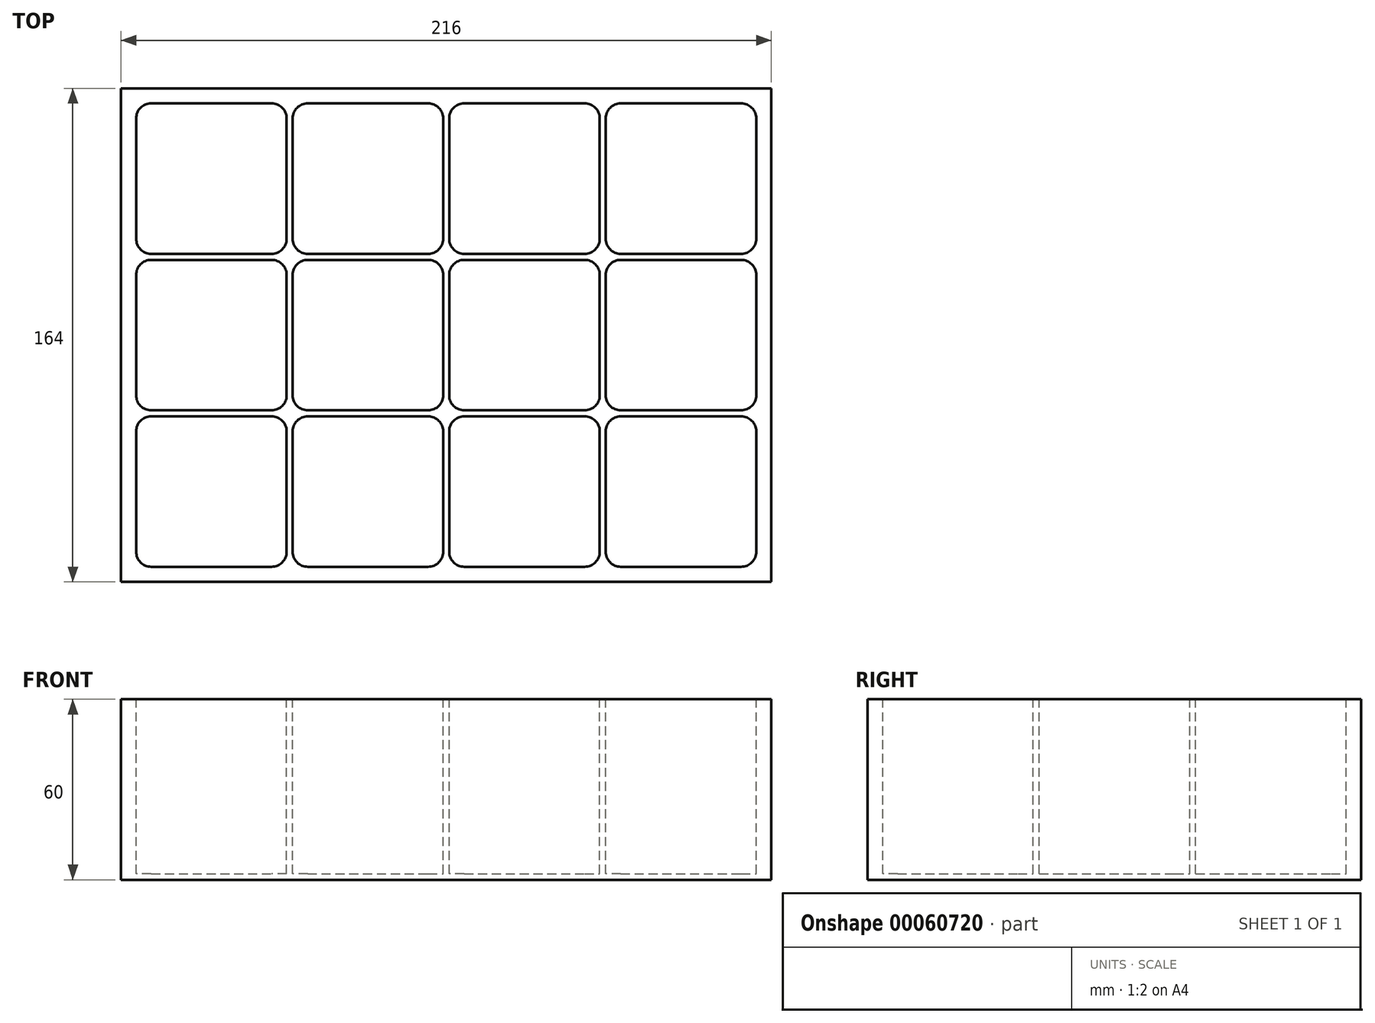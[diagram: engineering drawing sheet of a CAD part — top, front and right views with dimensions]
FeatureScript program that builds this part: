
annotation { "Feature Type Name" : "Feature", "Feature Type Description" : "" }
export const myFeature = defineFeature(function(context is Context, id is Id, definition is map)
    precondition{}
    {
        {
            var Q0;
            Q0=qCreatedBy(makeId("Top.planeOp"),FACE);
            var sketch = newSketch(context, id + "F0", { "sketchPlane" : qUnion([Q0])});
            skLineSegment(sketch, "E0.bottom", {"start": v(-104.23, -49.94) * mm, "end": v(111.77, -49.94) * mm});
            skLineSegment(sketch, "E0.top", {"start": v(-104.23, 114.06) * mm, "end": v(111.77, 114.06) * mm});
            skLineSegment(sketch, "E0.left", {"start": v(-104.23, -49.94) * mm, "end": v(-104.23, 114.06) * mm});
            skLineSegment(sketch, "E0.right", {"start": v(111.77, -49.94) * mm, "end": v(111.77, 114.06) * mm});
            skSolve(sketch);
        }
        {
            var Q0;
            Q0=makeQuery(id+"F0.imprint","IMPRINT",FACE,{"disambiguationData":[TD([[makeQuery(id+"F0.imprint","IMPRINT",EDGE,{"derivedFrom":sQuery(id+"F0.wireOp",EDGE,"E0.bottom")}),1.0]])]});
            extrude(context, id + "F1", {"entities" : qUnion([Q0]), "depth" : 60 * mm});
        }
        {
            var Q0;
            Q0=makeQuery(id+"F1.opExtrude","CAP_FACE",FACE,{"disambiguationData":[OSD([sQuery(id+"F0.wireOp",EDGE,"E0.bottom"),sQuery(id+"F0.wireOp",EDGE,"E0.top"),sQuery(id+"F0.wireOp",EDGE,"E0.left"),sQuery(id+"F0.wireOp",EDGE,"E0.right")])],"isStart":false});
            var sketch = newSketch(context, id + "F2", { "sketchPlane" : qUnion([Q0])});
            skLineSegment(sketch, "E1.bottom", {"start": v(-94.23, -44.94) * mm, "end": v(-54.23, -44.94) * mm});
            skLineSegment(sketch, "E1.top", {"start": v(-94.23, 5.06) * mm, "end": v(-54.23, 5.06) * mm});
            skLineSegment(sketch, "E1.left", {"start": v(-99.23, -39.94) * mm, "end": v(-99.23, 0.06) * mm});
            skLineSegment(sketch, "E1.right", {"start": v(-49.23, -39.94) * mm, "end": v(-49.23, 0.06) * mm});
            skPoint(sketch, "E2.visualSharp", {"position": v(-99.23, 5.06) * mm});
            skArc(sketch, "E2.filletArc", {"start": v(-94.23, 5.06) * mm, "mid": v(-97.76, 3.6) * mm, "end": v(-99.23, 0.06) * mm});
            skPoint(sketch, "E3.visualSharp", {"position": v(-49.23, 5.06) * mm});
            skArc(sketch, "E3.filletArc", {"start": v(-49.23, 0.06) * mm, "mid": v(-50.7, 3.6) * mm, "end": v(-54.23, 5.06) * mm});
            skPoint(sketch, "E4.visualSharp", {"position": v(-49.23, -44.94) * mm});
            skArc(sketch, "E4.filletArc", {"start": v(-54.23, -44.94) * mm, "mid": v(-50.7, -43.47) * mm, "end": v(-49.23, -39.94) * mm});
            skPoint(sketch, "E5.visualSharp", {"position": v(-99.23, -44.94) * mm});
            skArc(sketch, "E5.filletArc", {"start": v(-99.23, -39.94) * mm, "mid": v(-97.76, -43.47) * mm, "end": v(-94.23, -44.94) * mm});
            skLineSegment(sketch, "E6.0.1.0", {"start": v(-49.23, 12.06) * mm, "end": v(-49.23, 52.06) * mm});
            skArc(sketch, "E6.0.1.1", {"start": v(-54.23, 7.06) * mm, "mid": v(-50.7, 8.53) * mm, "end": v(-49.23, 12.06) * mm});
            skLineSegment(sketch, "E6.0.1.2", {"start": v(-94.23, 7.06) * mm, "end": v(-54.23, 7.06) * mm});
            skArc(sketch, "E6.0.1.3", {"start": v(-99.23, 12.06) * mm, "mid": v(-97.76, 8.53) * mm, "end": v(-94.23, 7.06) * mm});
            skLineSegment(sketch, "E6.0.1.4", {"start": v(-99.23, 12.06) * mm, "end": v(-99.23, 52.06) * mm});
            skArc(sketch, "E6.0.1.5", {"start": v(-94.23, 57.06) * mm, "mid": v(-97.76, 55.6) * mm, "end": v(-99.23, 52.06) * mm});
            skLineSegment(sketch, "E6.0.1.6", {"start": v(-94.23, 57.06) * mm, "end": v(-54.23, 57.06) * mm});
            skArc(sketch, "E6.0.1.7", {"start": v(-49.23, 52.06) * mm, "mid": v(-50.7, 55.6) * mm, "end": v(-54.23, 57.06) * mm});
            skLineSegment(sketch, "E6.0.2.0", {"start": v(-49.23, 64.06) * mm, "end": v(-49.23, 104.06) * mm});
            skArc(sketch, "E6.0.2.1", {"start": v(-54.23, 59.06) * mm, "mid": v(-50.7, 60.53) * mm, "end": v(-49.23, 64.06) * mm});
            skLineSegment(sketch, "E6.0.2.2", {"start": v(-94.23, 59.06) * mm, "end": v(-54.23, 59.06) * mm});
            skArc(sketch, "E6.0.2.3", {"start": v(-99.23, 64.06) * mm, "mid": v(-97.76, 60.53) * mm, "end": v(-94.23, 59.06) * mm});
            skLineSegment(sketch, "E6.0.2.4", {"start": v(-99.23, 64.06) * mm, "end": v(-99.23, 104.06) * mm});
            skArc(sketch, "E6.0.2.5", {"start": v(-94.23, 109.06) * mm, "mid": v(-97.76, 107.6) * mm, "end": v(-99.23, 104.06) * mm});
            skLineSegment(sketch, "E6.0.2.6", {"start": v(-94.23, 109.06) * mm, "end": v(-54.23, 109.06) * mm});
            skArc(sketch, "E6.0.2.7", {"start": v(-49.23, 104.06) * mm, "mid": v(-50.7, 107.6) * mm, "end": v(-54.23, 109.06) * mm});
            skLineSegment(sketch, "E6.1.0.0", {"start": v(2.77, -39.94) * mm, "end": v(2.77, 0.06) * mm});
            skArc(sketch, "E6.1.0.1", {"start": v(-2.23, -44.94) * mm, "mid": v(1.3, -43.47) * mm, "end": v(2.77, -39.94) * mm});
            skLineSegment(sketch, "E6.1.0.2", {"start": v(-42.23, -44.94) * mm, "end": v(-2.23, -44.94) * mm});
            skArc(sketch, "E6.1.0.3", {"start": v(-47.23, -39.94) * mm, "mid": v(-45.76, -43.47) * mm, "end": v(-42.23, -44.94) * mm});
            skLineSegment(sketch, "E6.1.0.4", {"start": v(-47.23, -39.94) * mm, "end": v(-47.23, 0.06) * mm});
            skArc(sketch, "E6.1.0.5", {"start": v(-42.23, 5.06) * mm, "mid": v(-45.76, 3.6) * mm, "end": v(-47.23, 0.06) * mm});
            skLineSegment(sketch, "E6.1.0.6", {"start": v(-42.23, 5.06) * mm, "end": v(-2.23, 5.06) * mm});
            skArc(sketch, "E6.1.0.7", {"start": v(2.77, 0.06) * mm, "mid": v(1.3, 3.6) * mm, "end": v(-2.23, 5.06) * mm});
            skLineSegment(sketch, "E6.1.1.0", {"start": v(2.77, 12.06) * mm, "end": v(2.77, 52.06) * mm});
            skArc(sketch, "E6.1.1.1", {"start": v(-2.23, 7.06) * mm, "mid": v(1.3, 8.53) * mm, "end": v(2.77, 12.06) * mm});
            skLineSegment(sketch, "E6.1.1.2", {"start": v(-42.23, 7.06) * mm, "end": v(-2.23, 7.06) * mm});
            skArc(sketch, "E6.1.1.3", {"start": v(-47.23, 12.06) * mm, "mid": v(-45.76, 8.53) * mm, "end": v(-42.23, 7.06) * mm});
            skLineSegment(sketch, "E6.1.1.4", {"start": v(-47.23, 12.06) * mm, "end": v(-47.23, 52.06) * mm});
            skArc(sketch, "E6.1.1.5", {"start": v(-42.23, 57.06) * mm, "mid": v(-45.76, 55.6) * mm, "end": v(-47.23, 52.06) * mm});
            skLineSegment(sketch, "E6.1.1.6", {"start": v(-42.23, 57.06) * mm, "end": v(-2.23, 57.06) * mm});
            skArc(sketch, "E6.1.1.7", {"start": v(2.77, 52.06) * mm, "mid": v(1.3, 55.6) * mm, "end": v(-2.23, 57.06) * mm});
            skLineSegment(sketch, "E6.1.2.0", {"start": v(2.77, 64.06) * mm, "end": v(2.77, 104.06) * mm});
            skArc(sketch, "E6.1.2.1", {"start": v(-2.23, 59.06) * mm, "mid": v(1.3, 60.53) * mm, "end": v(2.77, 64.06) * mm});
            skLineSegment(sketch, "E6.1.2.2", {"start": v(-42.23, 59.06) * mm, "end": v(-2.23, 59.06) * mm});
            skArc(sketch, "E6.1.2.3", {"start": v(-47.23, 64.06) * mm, "mid": v(-45.76, 60.53) * mm, "end": v(-42.23, 59.06) * mm});
            skLineSegment(sketch, "E6.1.2.4", {"start": v(-47.23, 64.06) * mm, "end": v(-47.23, 104.06) * mm});
            skArc(sketch, "E6.1.2.5", {"start": v(-42.23, 109.06) * mm, "mid": v(-45.76, 107.6) * mm, "end": v(-47.23, 104.06) * mm});
            skLineSegment(sketch, "E6.1.2.6", {"start": v(-42.23, 109.06) * mm, "end": v(-2.23, 109.06) * mm});
            skArc(sketch, "E6.1.2.7", {"start": v(2.77, 104.06) * mm, "mid": v(1.3, 107.6) * mm, "end": v(-2.23, 109.06) * mm});
            skLineSegment(sketch, "E6.2.0.0", {"start": v(54.77, -39.94) * mm, "end": v(54.77, 0.06) * mm});
            skArc(sketch, "E6.2.0.1", {"start": v(49.77, -44.94) * mm, "mid": v(53.3, -43.47) * mm, "end": v(54.77, -39.94) * mm});
            skLineSegment(sketch, "E6.2.0.2", {"start": v(9.77, -44.94) * mm, "end": v(49.77, -44.94) * mm});
            skArc(sketch, "E6.2.0.3", {"start": v(4.77, -39.94) * mm, "mid": v(6.24, -43.47) * mm, "end": v(9.77, -44.94) * mm});
            skLineSegment(sketch, "E6.2.0.4", {"start": v(4.77, -39.94) * mm, "end": v(4.77, 0.06) * mm});
            skArc(sketch, "E6.2.0.5", {"start": v(9.77, 5.06) * mm, "mid": v(6.24, 3.6) * mm, "end": v(4.77, 0.06) * mm});
            skLineSegment(sketch, "E6.2.0.6", {"start": v(9.77, 5.06) * mm, "end": v(49.77, 5.06) * mm});
            skArc(sketch, "E6.2.0.7", {"start": v(54.77, 0.06) * mm, "mid": v(53.3, 3.6) * mm, "end": v(49.77, 5.06) * mm});
            skLineSegment(sketch, "E6.2.1.0", {"start": v(54.77, 12.06) * mm, "end": v(54.77, 52.06) * mm});
            skArc(sketch, "E6.2.1.1", {"start": v(49.77, 7.06) * mm, "mid": v(53.3, 8.53) * mm, "end": v(54.77, 12.06) * mm});
            skLineSegment(sketch, "E6.2.1.2", {"start": v(9.77, 7.06) * mm, "end": v(49.77, 7.06) * mm});
            skArc(sketch, "E6.2.1.3", {"start": v(4.77, 12.06) * mm, "mid": v(6.24, 8.53) * mm, "end": v(9.77, 7.06) * mm});
            skLineSegment(sketch, "E6.2.1.4", {"start": v(4.77, 12.06) * mm, "end": v(4.77, 52.06) * mm});
            skArc(sketch, "E6.2.1.5", {"start": v(9.77, 57.06) * mm, "mid": v(6.24, 55.6) * mm, "end": v(4.77, 52.06) * mm});
            skLineSegment(sketch, "E6.2.1.6", {"start": v(9.77, 57.06) * mm, "end": v(49.77, 57.06) * mm});
            skArc(sketch, "E6.2.1.7", {"start": v(54.77, 52.06) * mm, "mid": v(53.3, 55.6) * mm, "end": v(49.77, 57.06) * mm});
            skLineSegment(sketch, "E6.2.2.0", {"start": v(54.77, 64.06) * mm, "end": v(54.77, 104.06) * mm});
            skArc(sketch, "E6.2.2.1", {"start": v(49.77, 59.06) * mm, "mid": v(53.3, 60.53) * mm, "end": v(54.77, 64.06) * mm});
            skLineSegment(sketch, "E6.2.2.2", {"start": v(9.77, 59.06) * mm, "end": v(49.77, 59.06) * mm});
            skArc(sketch, "E6.2.2.3", {"start": v(4.77, 64.06) * mm, "mid": v(6.24, 60.53) * mm, "end": v(9.77, 59.06) * mm});
            skLineSegment(sketch, "E6.2.2.4", {"start": v(4.77, 64.06) * mm, "end": v(4.77, 104.06) * mm});
            skArc(sketch, "E6.2.2.5", {"start": v(9.77, 109.06) * mm, "mid": v(6.24, 107.6) * mm, "end": v(4.77, 104.06) * mm});
            skLineSegment(sketch, "E6.2.2.6", {"start": v(9.77, 109.06) * mm, "end": v(49.77, 109.06) * mm});
            skArc(sketch, "E6.2.2.7", {"start": v(54.77, 104.06) * mm, "mid": v(53.3, 107.6) * mm, "end": v(49.77, 109.06) * mm});
            skLineSegment(sketch, "E6.3.0.0", {"start": v(106.77, -39.94) * mm, "end": v(106.77, 0.06) * mm});
            skArc(sketch, "E6.3.0.1", {"start": v(101.77, -44.94) * mm, "mid": v(105.3, -43.47) * mm, "end": v(106.77, -39.94) * mm});
            skLineSegment(sketch, "E6.3.0.2", {"start": v(61.77, -44.94) * mm, "end": v(101.77, -44.94) * mm});
            skArc(sketch, "E6.3.0.3", {"start": v(56.77, -39.94) * mm, "mid": v(58.24, -43.47) * mm, "end": v(61.77, -44.94) * mm});
            skLineSegment(sketch, "E6.3.0.4", {"start": v(56.77, -39.94) * mm, "end": v(56.77, 0.06) * mm});
            skArc(sketch, "E6.3.0.5", {"start": v(61.77, 5.06) * mm, "mid": v(58.24, 3.6) * mm, "end": v(56.77, 0.06) * mm});
            skLineSegment(sketch, "E6.3.0.6", {"start": v(61.77, 5.06) * mm, "end": v(101.77, 5.06) * mm});
            skArc(sketch, "E6.3.0.7", {"start": v(106.77, 0.06) * mm, "mid": v(105.3, 3.6) * mm, "end": v(101.77, 5.06) * mm});
            skLineSegment(sketch, "E6.3.1.0", {"start": v(106.77, 12.06) * mm, "end": v(106.77, 52.06) * mm});
            skArc(sketch, "E6.3.1.1", {"start": v(101.77, 7.06) * mm, "mid": v(105.3, 8.53) * mm, "end": v(106.77, 12.06) * mm});
            skLineSegment(sketch, "E6.3.1.2", {"start": v(61.77, 7.06) * mm, "end": v(101.77, 7.06) * mm});
            skArc(sketch, "E6.3.1.3", {"start": v(56.77, 12.06) * mm, "mid": v(58.24, 8.53) * mm, "end": v(61.77, 7.06) * mm});
            skLineSegment(sketch, "E6.3.1.4", {"start": v(56.77, 12.06) * mm, "end": v(56.77, 52.06) * mm});
            skArc(sketch, "E6.3.1.5", {"start": v(61.77, 57.06) * mm, "mid": v(58.24, 55.6) * mm, "end": v(56.77, 52.06) * mm});
            skLineSegment(sketch, "E6.3.1.6", {"start": v(61.77, 57.06) * mm, "end": v(101.77, 57.06) * mm});
            skArc(sketch, "E6.3.1.7", {"start": v(106.77, 52.06) * mm, "mid": v(105.3, 55.6) * mm, "end": v(101.77, 57.06) * mm});
            skLineSegment(sketch, "E6.3.2.0", {"start": v(106.77, 64.06) * mm, "end": v(106.77, 104.06) * mm});
            skArc(sketch, "E6.3.2.1", {"start": v(101.77, 59.06) * mm, "mid": v(105.3, 60.53) * mm, "end": v(106.77, 64.06) * mm});
            skLineSegment(sketch, "E6.3.2.2", {"start": v(61.77, 59.06) * mm, "end": v(101.77, 59.06) * mm});
            skArc(sketch, "E6.3.2.3", {"start": v(56.77, 64.06) * mm, "mid": v(58.24, 60.53) * mm, "end": v(61.77, 59.06) * mm});
            skLineSegment(sketch, "E6.3.2.4", {"start": v(56.77, 64.06) * mm, "end": v(56.77, 104.06) * mm});
            skArc(sketch, "E6.3.2.5", {"start": v(61.77, 109.06) * mm, "mid": v(58.24, 107.6) * mm, "end": v(56.77, 104.06) * mm});
            skLineSegment(sketch, "E6.3.2.6", {"start": v(61.77, 109.06) * mm, "end": v(101.77, 109.06) * mm});
            skArc(sketch, "E6.3.2.7", {"start": v(106.77, 104.06) * mm, "mid": v(105.3, 107.6) * mm, "end": v(101.77, 109.06) * mm});
            skLineSegment(sketch, "E6.direction1", {"start": v(-49.23, -39.94) * mm, "end": v(2.77, -39.94) * mm, "construction": true});
            skLineSegment(sketch, "E6.direction2", {"start": v(-49.23, -39.94) * mm, "end": v(-49.23, 12.06) * mm, "construction": true});
            skSolve(sketch);
        }
        {
            var Q0;
            Q0 = qSketchRegion(id + "F2", true);
            extrude(context, id + "F3", {"entities" : qUnion([Q0]), "operationType" : NewBodyOperationType.REMOVE, "oppositeDirection" : true, "depth" : 58 * mm});
        }
    });
